# Revit family: Eelectron_Compact_USB_Interface_PC_KNX
name_source: partatom
category: Electrical Equipment
revit_build: Autodesk Revit 2016 (Build: 20161004_0715(x64)
units: mm (PartAtom-declared; Revit-internal decimal feet)

## family parameters
Cut with Voids When Loaded = No
Host = Face
Part Type = Other Panel
Room Calculation Point = No
Round Connector Dimension = Use Diameter
Shared = No

## types (1)
- IN00A03USB
    CE marking = EMC directive 2014 / 30 / EU
RoHS directive 2011 / 65 / EU
EN 50491-3: 2009
EN 50491-5-1: 2010
EN 50491-5-2: 2010
EN 50491-5-3: 2010
EN 61000-6-2: 2005
EN 61000-6-3: 2007 + A1: 2011
EN 50581: 2012
    Connectors = Connector for KNX TP Bus (red/black)
USB: Connector type B
max. cable length: 5 m
    Date of publishing = 13/03/2018
    Default Elevation = 1219.2 mm  [stored 4 ft]
    Description = Compact USB Interface between PC and KNX
    Dimensions = 1 unit (18 mm)
    Edition number = rev. 0.0
    Housing = Plastic (PC)
    Indicators = 2 LEDs, multicolor
    KNX = Medium TP
Interface protocol: HID/cEMI
Max. APDU length: 55
Device model: System B
    Manufacturer = Eelectron S.p.a.
    Max Ambient temperature = 45 °C
    Max Storage temperature = 70 °C
    Min Ambient temperature = -551 °C
    Min Storage temperature = -571 °C
    Model = IN00A03USB
    Protection class = (acc. EN 60529): IP 20
    Weight = 0.04 kg

note: [stored X ft] marks values corroborated as IEEE doubles in the binary element streams (Revit-internal decimal feet)
